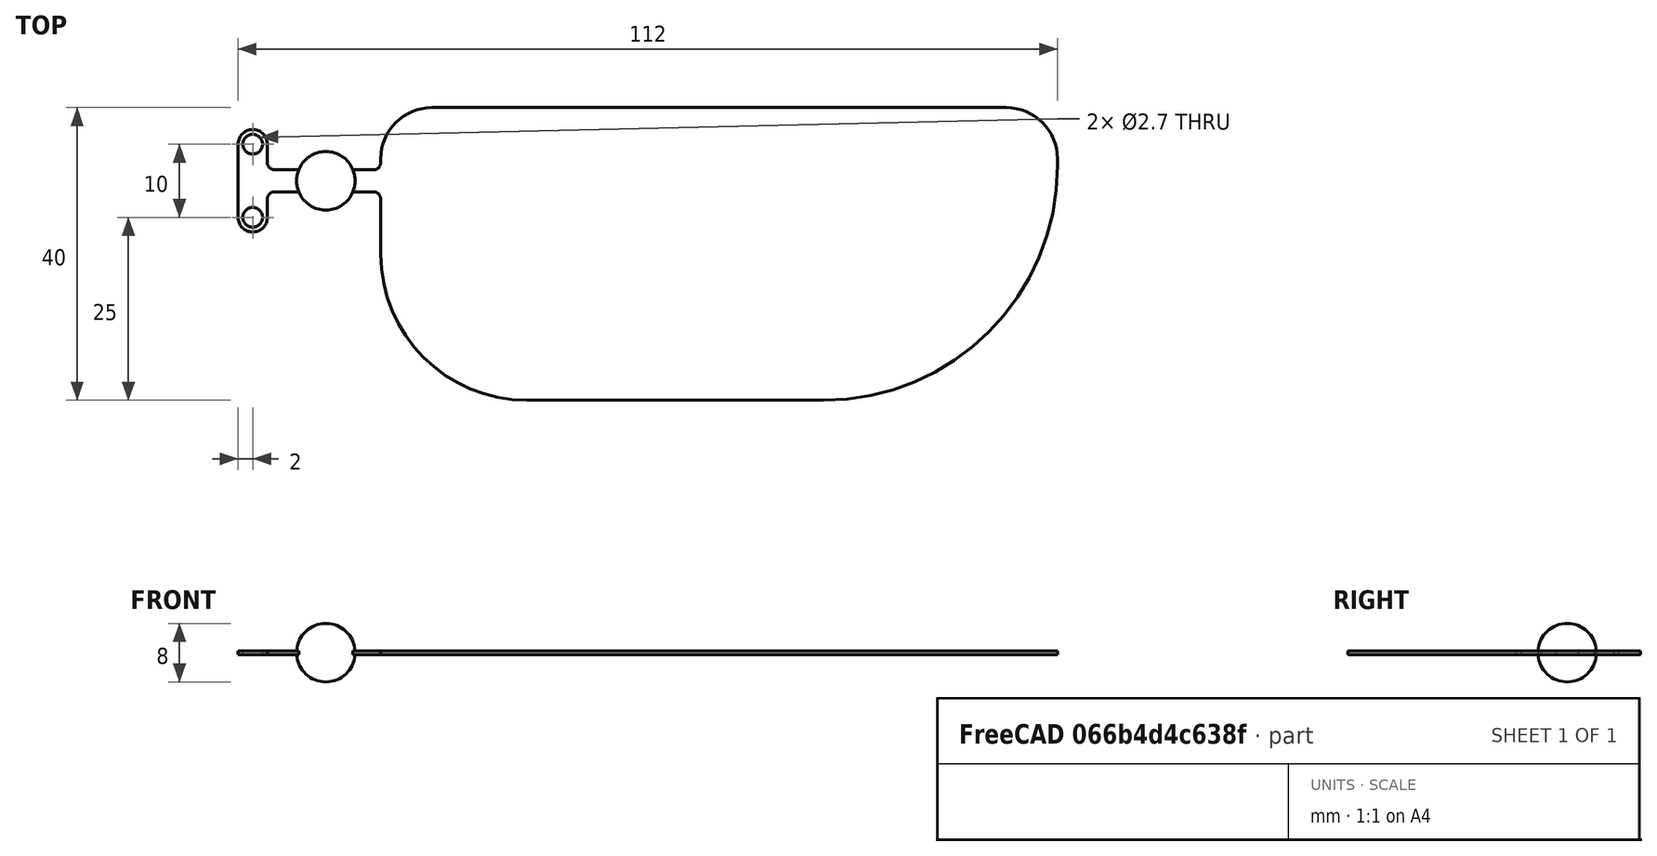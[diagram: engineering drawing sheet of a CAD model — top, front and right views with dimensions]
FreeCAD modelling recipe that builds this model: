
FCSTD DOCUMENT  (FreeCAD 0.19R24366 (Git))
Label: wing
License: All rights reserved
LicenseURL: http://en.wikipedia.org/wiki/All_rights_reserved
objects: PartDesign::Fillet×5, Sketcher::SketchObject×4, PartDesign::Pad×3, Spreadsheet::Sheet×1, PartDesign::Revolution×1, PartDesign::Body×1, Mesh::Feature×1
note: 23 computed .brp shape members not serialized (recipe doc carries the construction recipe); baked Part::Feature solids carry a one-line shape summary decoded from their .brp

FEATURE [Spreadsheet::Sheet] Spreadsheet
  cells = A1=BallDiameter; B1(BallDiameter)==8mm; A2=Length; B2(Length)==100mm; A3=Chord; B3(Chord)==40mm; A4=AxisAsFractionOfChord; B4(AxisAsFractionOfChord)=0.25; A5=BaseCutout; B5(BaseCutout)==7.5mm; A6=UpperTipFilletRadius; B6(UpperTipFilletRadius)==7mm; A7=LowerTipFilletRadius; B7(LowerTipFilletRadius)==32mm; A8=UpperBaseFilletRadius; B8(UpperBaseFilletRadius)==7mm; A9=LowerBaseFilletRadius; B9(LowerBaseFilletRadius)==20mm; A10=BaseWidth; B10(BaseWidth)==3mm; A11=Thickness; B11(Thickness)==0.5mm; A12=ActuatorDistance; B12(ActuatorDistance)==10mm; A13=ActuatorSeparation; B13(ActuatorSeparation)==10mm; A14=ActuatorAttachmentWidth; B14(ActuatorAttachmentWidth)==4mm; A15=RodBallHoleDiameter; B15(RodBallHoleDiameter)==2.7mm; A16=BaseFilletRadius; B16(BaseFilletRadius)==1mm
FEATURE [Sketcher::SketchObject] Sketch
  FullyConstrained = true
  MapMode = 5
  Support = -> [XY_Plane]
  expr: Constraints[7] = 0.5 * Spreadsheet.BallDiameter
  sketch-geometry (3):
    g0: ArcOfCircle CenterX=0 CenterY=0 CenterZ=0 NormalX=0 NormalY=0 NormalZ=1 AngleXU=0 Radius=4 StartAngle=0 EndAngle=3.14159
    g1: LineSegment StartX=-4 StartY=-1.3e-15 StartZ=0 EndX=0 EndY=0 EndZ=0
    g2: LineSegment StartX=0 StartY=0 StartZ=0 EndX=4 EndY=0 EndZ=0
  constraints (8):
    c: Coincident(g0,g-1)
    c: PointOnObject(g0,g-1)
    c: PointOnObject(g0,g-1)
    c: Coincident(g1,g2)
    c: Coincident(g0,g1)
    c: Coincident(g0,g1)
    c: Coincident(g2,g0)
    c: Radius(g0) = 4
FEATURE [PartDesign::Revolution] Revolution
  Angle = 360
  Axis = (1,0,0)
  Base = (0,0,0)
  Profile = -> Sketch
  ReferenceAxis = -> X_Axis
FEATURE [Sketcher::SketchObject] Sketch001
  FullyConstrained = true
  MapMode = 5
  Support = -> [XY_Plane]
  expr: Constraints[12] = Spreadsheet.BaseCutout
  expr: Constraints[13] = Spreadsheet.BaseWidth
  sketch-geometry (5):
    g0: LineSegment StartX=0 StartY=0 StartZ=0 EndX=0 EndY=1.5 EndZ=0
    g1: LineSegment StartX=0 StartY=1.5 StartZ=0 EndX=7.5 EndY=1.5 EndZ=0
    g2: LineSegment StartX=7.5 StartY=1.5 StartZ=0 EndX=7.5 EndY=-1.5 EndZ=0
    g3: LineSegment StartX=7.5 StartY=-1.5 StartZ=0 EndX=0 EndY=-1.5 EndZ=0
    g4: LineSegment StartX=0 StartY=-1.5 StartZ=0 EndX=0 EndY=0 EndZ=0
  constraints (14):
    c: Vertical(g0)
    c: Coincident(g0,g1)
    c: Horizontal(g1)
    c: Coincident(g1,g2)
    c: Vertical(g2)
    c: Coincident(g2,g3)
    c: Horizontal(g3)
    c: Coincident(g3,g4)
    c: Vertical(g4)
    c: Coincident(g4,g0)
    c: Coincident(g4,g-1)
    c: Equal(g4,g0)
    c: Distance(g1) = 7.5
    c: Distance(g2) = 3
FEATURE [PartDesign::Pad] Pad
  BaseFeature = -> Revolution
  Direction = (1,1,1)
  Length = 0.5
  Length2 = 100
  Midplane = true
  Profile = -> Sketch001
  Type = 0
  expr: Length = Spreadsheet.Thickness
FEATURE [Sketcher::SketchObject] Sketch002
  FullyConstrained = true
  MapMode = 5
  Support = -> [XY_Plane]
  expr: Constraints[8] = Spreadsheet.Chord
  expr: Constraints[9] = Spreadsheet.Length - Spreadsheet.BaseCutout
  expr: Constraints[17] = Spreadsheet.BaseCutout
  expr: Constraints[13] = Spreadsheet.AxisAsFractionOfChord * Spreadsheet.Chord
  sketch-geometry (6):
    g0: LineSegment StartX=7.5 StartY=10 StartZ=0 EndX=100 EndY=10 EndZ=0
    g1: LineSegment StartX=100 StartY=10 StartZ=0 EndX=100 EndY=-30 EndZ=0
    g2: LineSegment StartX=100 StartY=-30 StartZ=0 EndX=7.5 EndY=-30 EndZ=0
    g3: LineSegment StartX=7.5 StartY=-30 StartZ=0 EndX=7.5 EndY=10 EndZ=0
    g4: LineSegment StartX=7.5 StartY=0 StartZ=0 EndX=100 EndY=0 EndZ=0
    g5: LineSegment StartX=0 StartY=0 StartZ=0 EndX=7.5 EndY=0 EndZ=0
  constraints (18):
    c: Coincident(g0,g1)
    c: Coincident(g1,g2)
    c: Coincident(g2,g3)
    c: Coincident(g3,g0)
    c: Horizontal(g0)
    c: Horizontal(g2)
    c: Vertical(g1)
    c: Vertical(g3)
    c: Distance(g1) = 40
    c: Distance(g2) = 92.5
    c: Horizontal(g4)
    c: PointOnObject(g4,g3)
    c: PointOnObject(g4,g1)
    c: Distance(g4,g0) = 10
    c: Horizontal(g5)
    c: Coincident(g5,g-1)
    c: Coincident(g5,g4)
    c: Distance(g5) = 7.5
FEATURE [PartDesign::Pad] Pad001
  BaseFeature = -> Pad
  Direction = (1,1,1)
  Length = 0.5
  Length2 = 100
  Midplane = true
  Profile = -> Sketch002
  Type = 0
  expr: Length = Spreadsheet.Thickness
FEATURE [Sketcher::SketchObject] Sketch003
  FullyConstrained = true
  MapMode = 5
  Support = -> [XY_Plane]
  expr: Constraints[40] = Spreadsheet.RodBallHoleDiameter
  expr: Constraints[33] = Spreadsheet.ActuatorDistance
  expr: Constraints[34] = Spreadsheet.BaseWidth
  expr: Constraints[36] = Spreadsheet.ActuatorAttachmentWidth
  expr: Constraints[35] = Spreadsheet.ActuatorSeparation
  sketch-geometry (15):
    g0: LineSegment StartX=0 StartY=0 StartZ=0 EndX=0 EndY=1.5 EndZ=0
    g1: LineSegment StartX=0 StartY=1.5 StartZ=0 EndX=-8 EndY=1.5 EndZ=0
    g2: LineSegment StartX=-8 StartY=1.5 StartZ=0 EndX=-8 EndY=5 EndZ=0
    g3: LineSegment StartX=-8 StartY=5 StartZ=0 EndX=-12 EndY=5 EndZ=0
    g4: LineSegment StartX=-12 StartY=5 StartZ=0 EndX=-12 EndY=-5 EndZ=0
    g5: LineSegment StartX=-12 StartY=-5 StartZ=0 EndX=-8 EndY=-5 EndZ=0
    g6: LineSegment StartX=-8 StartY=-5 StartZ=0 EndX=-8 EndY=-1.5 EndZ=0
    g7: LineSegment StartX=-8 StartY=-1.5 StartZ=0 EndX=0 EndY=-1.5 EndZ=0
    g8: LineSegment StartX=0 StartY=-1.5 StartZ=0 EndX=0 EndY=0 EndZ=0
    g9: ArcOfCircle CenterX=-10 CenterY=5 CenterZ=0 NormalX=0 NormalY=0 NormalZ=1 AngleXU=0 Radius=2 StartAngle=0 EndAngle=3.14159
    g10: ArcOfCircle CenterX=-10 CenterY=-5 CenterZ=0 NormalX=0 NormalY=0 NormalZ=1 AngleXU=0 Radius=2 StartAngle=3.14159 EndAngle=6.28319
    g11: LineSegment StartX=-10 StartY=5 StartZ=0 EndX=-10 EndY=0 EndZ=0
    g12: LineSegment StartX=-10 StartY=0 StartZ=0 EndX=-10 EndY=-5 EndZ=0
    g13: Circle CenterX=-10 CenterY=5 CenterZ=0 NormalX=0 NormalY=0 NormalZ=1 AngleXU=0 Radius=1.35
    g14: Circle CenterX=-10 CenterY=-5 CenterZ=0 NormalX=0 NormalY=0 NormalZ=1 AngleXU=0 Radius=1.35
  constraints (41):
    c: Vertical(g0)
    c: Coincident(g0,g1)
    c: Horizontal(g1)
    c: Coincident(g1,g2)
    c: Vertical(g2)
    c: Coincident(g2,g3)
    c: Horizontal(g3)
    c: Coincident(g3,g4)
    c: Vertical(g4)
    c: Coincident(g4,g5)
    c: Horizontal(g5)
    c: Coincident(g5,g6)
    c: Vertical(g6)
    c: Coincident(g6,g7)
    c: Horizontal(g7)
    c: Coincident(g7,g8)
    c: Vertical(g8)
    c: Coincident(g8,g0)
    c: Coincident(g8,g-1)
    c: Equal(g0,g8)
    c: Equal(g2,g6)
    c: Equal(g1,g7)
    c: Coincident(g9,g3)
    c: Coincident(g9,g2)
    c: PointOnObject(g9,g3)
    c: Coincident(g10,g4)
    c: Coincident(g10,g5)
    c: PointOnObject(g10,g5)
    c: Vertical(g11)
    c: Coincident(g11,g12)
    c: Equal(g11,g12)
    c: Coincident(g11,g9)
    c: Coincident(g12,g10)
    c: Distance(g11,g0) = 10
    c: Distance(g0,g7) = 3
    c: Distance(g9,g10) = 10
    c: Distance(g4,g6) = 4
    c: Coincident(g13,g9)
    c: Coincident(g14,g10)
    c: Equal(g13,g14)
    c: Diameter(g13) = 2.7
FEATURE [PartDesign::Pad] Pad002
  BaseFeature = -> Pad001
  Direction = (1,1,1)
  Length = 0.5
  Length2 = 100
  Midplane = true
  Profile = -> Sketch003
  Type = 0
  expr: Length = Spreadsheet.Thickness
FEATURE [PartDesign::Fillet] Fillet
  Base = -> Pad002 [Edge2]
  BaseFeature = -> Pad002
  Radius = 7
  SupportTransform = false
  expr: Radius = Spreadsheet.UpperTipFilletRadius
FEATURE [PartDesign::Fillet] Fillet001
  Base = -> Fillet [Edge19]
  BaseFeature = -> Fillet
  Radius = 32
  SupportTransform = false
  expr: Radius = Spreadsheet.LowerTipFilletRadius
FEATURE [PartDesign::Fillet] Fillet002
  Base = -> Fillet001 [Edge16]
  BaseFeature = -> Fillet001
  Radius = 20
  SupportTransform = false
  expr: Radius = Spreadsheet.LowerBaseFilletRadius
FEATURE [PartDesign::Fillet] Fillet003
  Base = -> Fillet002 [Edge26]
  BaseFeature = -> Fillet002
  Radius = 7
  SupportTransform = false
  expr: Radius = Spreadsheet.UpperBaseFilletRadius
FEATURE [PartDesign::Fillet] Fillet004
  Base = -> Fillet003 [Edge58,Edge47,Edge12,Edge22]
  BaseFeature = -> Fillet003
  Radius = 1
  SupportTransform = false
FEATURE [PartDesign::Body] Body
  Group = -> [Sketch,Revolution,Sketch001,Pad,Sketch002,Pad001,Sketch003,Pad002,Fillet,Fillet001,Fillet002,Fillet003,Fillet004]
  Origin = -> Origin
  Tip = -> Fillet004
FEATURE [Mesh::Feature] Mesh  label="Fillet004 (Meshed)"
